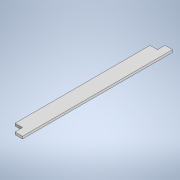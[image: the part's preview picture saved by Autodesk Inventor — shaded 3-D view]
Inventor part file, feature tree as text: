
AUTODESK INVENTOR PART (.ipt)
format: ipt  version: 2020 (Build 240168000, 168)  size: 107,008 bytes
history: native  units: mm
features: other x1, extrude x1, sketch x1
ambient origin geometry x8: Origin, YZ Plane, XZ Plane, XY Plane, X Axis, Y Axis, Z Axis, Center Point
bodies: Solid1 (feature_tree)
feature tree (3):
  other  "<userpath>\Documents\Development\paragon-printer\Paragon Printer Parameters.xlsx"
  extrude  "Extrusion1"  Depth=20.0mm
  sketch  "Sketch1"  dims[d0=400.0mm d1=20.0mm d2=20.0mm d3=20.0mm d4=20.0mm d5=40.0mm d6=6.35mm d7=0.0mm]
